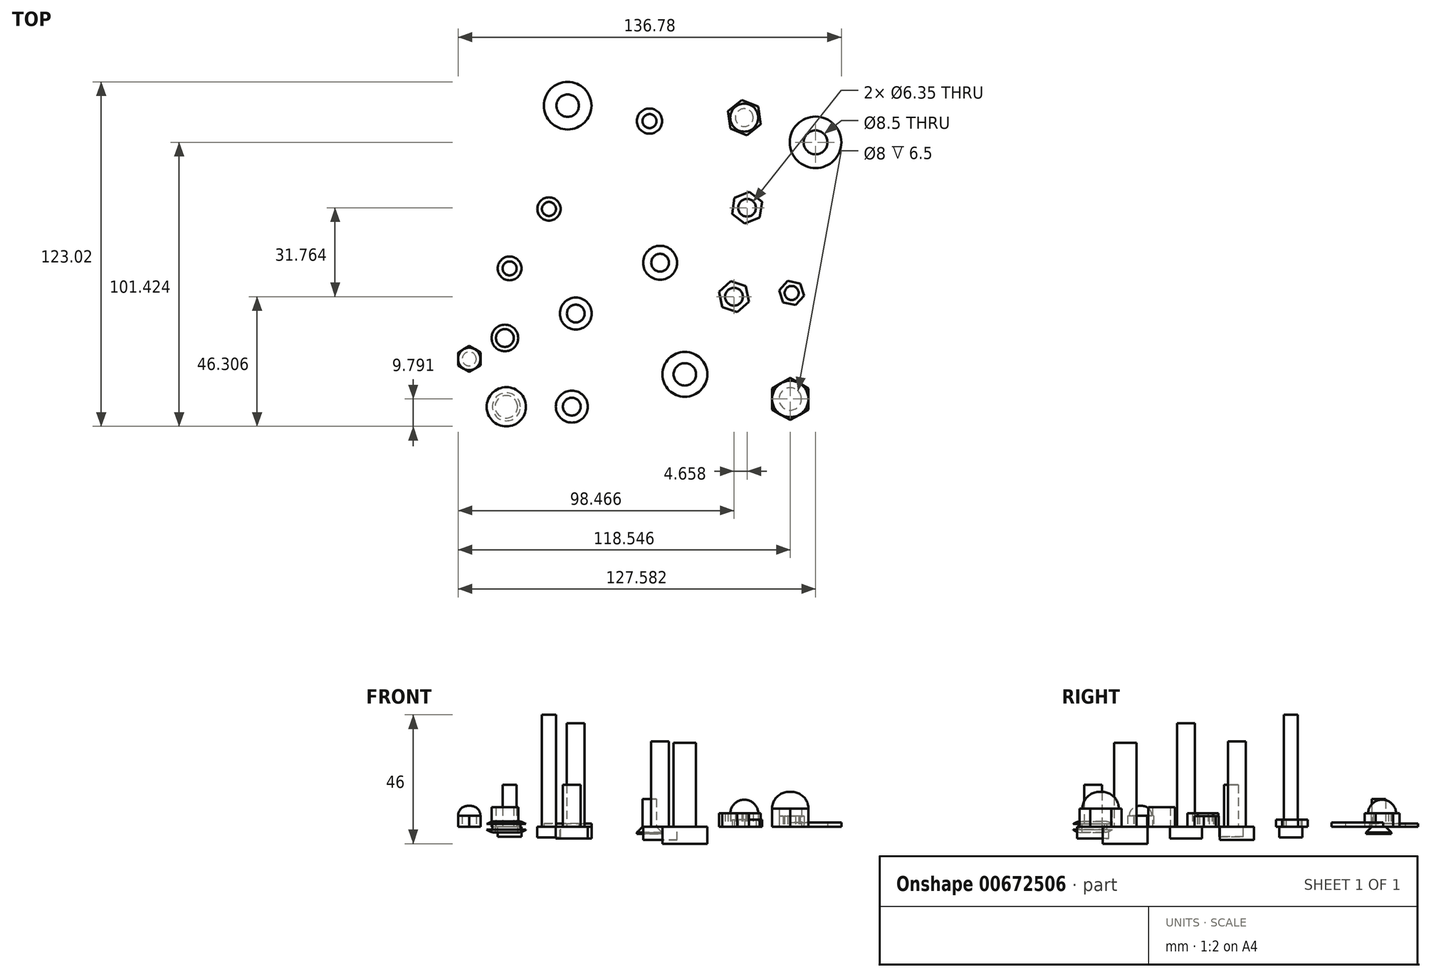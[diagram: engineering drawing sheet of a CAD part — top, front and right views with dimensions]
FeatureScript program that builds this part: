
annotation { "Feature Type Name" : "Feature", "Feature Type Description" : "" }
export const myFeature = defineFeature(function(context is Context, id is Id, definition is map)
    precondition{}
    {
        {
            var Q0;
            Q0=qCreatedBy(makeId("Top.planeOp"),FACE);
            var sketch = newSketch(context, id + "F0", { "sketchPlane" : qUnion([Q0])});
            skCircle(sketch, "E0", {"center": v(0, 0) * mm, "radius": 3.18 * mm});
            skSolve(sketch);
        }
        {
            var Q0;
            Q0 = qSketchRegion(id + "F0", true);
            extrude(context, id + "F1", {"entities" : qUnion([Q0]), "depth" : 30.5 * mm, "offsetDistance" : 25 * mm});
        }
        {
            var Q0;
            Q0=makeQuery(id+"F1.opExtrude","CAP_FACE",FACE,{"disambiguationData":[OSD([sQuery(id+"F0.wireOp",EDGE,"E0")])],"isStart":true});
            var sketch = newSketch(context, id + "F2", { "sketchPlane" : qUnion([Q0])});
            skCircle(sketch, "E1", {"center": v(0, 0) * mm, "radius": 6.07 * mm});
            skSolve(sketch);
        }
        {
            var Q0;
            Q0 = qSketchRegion(id + "F2", true);
            extrude(context, id + "F3", {"entities" : qUnion([Q0]), "operationType" : NewBodyOperationType.ADD, "depth" : 4.7 * mm, "offsetDistance" : 25 * mm});
        }
        {
            var Q0;
            Q0=qCreatedBy(makeId("Top.planeOp"),FACE);
            var sketch = newSketch(context, id + "F4", { "sketchPlane" : qUnion([Q0])});
            skCircle(sketch, "E2.cCircle", {"center": v(26.36, -12.11) * mm, "radius": 4.9 * mm, "construction": true});
            skLineSegment(sketch, "E2.0", {"start": v(21, -10.32) * mm, "end": v(25.23, -6.57) * mm});
            skLineSegment(sketch, "E2.1", {"start": v(25.23, -6.57) * mm, "end": v(30.6, -8.37) * mm});
            skLineSegment(sketch, "E2.2", {"start": v(30.6, -8.37) * mm, "end": v(31.72, -13.91) * mm});
            skLineSegment(sketch, "E2.3", {"start": v(31.72, -13.91) * mm, "end": v(27.48, -17.66) * mm});
            skLineSegment(sketch, "E2.4", {"start": v(27.48, -17.66) * mm, "end": v(22.12, -15.86) * mm});
            skLineSegment(sketch, "E2.5", {"start": v(22.12, -15.86) * mm, "end": v(21, -10.32) * mm});
            skPoint(sketch, "E2.0.midPoint", {"position": v(23.11, -8.44) * mm});
            skCircle(sketch, "E3", {"center": v(26.36, -12.11) * mm, "radius": 3.17 * mm});
            skSolve(sketch);
        }
        {
            var Q0;
            Q0 = qSketchRegion(id + "F4", true);
            extrude(context, id + "F5", {"entities" : qUnion([Q0]), "depth" : 4.9 * mm, "offsetDistance" : 25 * mm});
        }
        {
            var Q0;
            Q0=qCreatedBy(makeId("Top.planeOp"),FACE);
            var sketch = newSketch(context, id + "F6", { "sketchPlane" : qUnion([Q0])});
            skCircle(sketch, "E4", {"center": v(-30.1, -18.13) * mm, "radius": 3.17 * mm});
            skSolve(sketch);
        }
        {
            var Q0;
            Q0 = qSketchRegion(id + "F6", true);
            extrude(context, id + "F7", {"entities" : qUnion([Q0]), "depth" : 37 * mm, "offsetDistance" : 25 * mm});
        }
        {
            var Q0;
            Q0=makeQuery(id+"F7.opExtrude","CAP_FACE",FACE,{"disambiguationData":[OSD([sQuery(id+"F6.wireOp",EDGE,"E4")])],"isStart":true});
            var sketch = newSketch(context, id + "F8", { "sketchPlane" : qUnion([Q0])});
            skCircle(sketch, "E5", {"center": v(-30.1, 18.13) * mm, "radius": 5.7 * mm});
            skSolve(sketch);
        }
        {
            var Q0;
            Q0 = qSketchRegion(id + "F8", true);
            extrude(context, id + "F9", {"entities" : qUnion([Q0]), "operationType" : NewBodyOperationType.ADD, "depth" : 4.1 * mm, "offsetDistance" : 25 * mm});
        }
        {
            var Q0;
            Q0=qCreatedBy(makeId("Top.planeOp"),FACE);
            var sketch = newSketch(context, id + "F10", { "sketchPlane" : qUnion([Q0])});
            skCircle(sketch, "E6.cCircle", {"center": v(31.01, 19.65) * mm, "radius": 4.97 * mm, "construction": true});
            skLineSegment(sketch, "E6.0", {"start": v(31.81, 25.34) * mm, "end": v(36.34, 21.8) * mm});
            skLineSegment(sketch, "E6.1", {"start": v(36.34, 21.8) * mm, "end": v(35.54, 16.12) * mm});
            skLineSegment(sketch, "E6.2", {"start": v(35.54, 16.12) * mm, "end": v(30.22, 13.96) * mm});
            skLineSegment(sketch, "E6.3", {"start": v(30.22, 13.96) * mm, "end": v(25.69, 17.5) * mm});
            skLineSegment(sketch, "E6.4", {"start": v(25.69, 17.5) * mm, "end": v(26.49, 23.18) * mm});
            skLineSegment(sketch, "E6.5", {"start": v(26.49, 23.18) * mm, "end": v(31.81, 25.34) * mm});
            skPoint(sketch, "E6.0.midPoint", {"position": v(34.07, 23.57) * mm});
            skCircle(sketch, "E7", {"center": v(31.01, 19.65) * mm, "radius": 3.17 * mm});
            skSolve(sketch);
        }
        {
            var Q0;
            Q0 = qSketchRegion(id + "F10", true);
            extrude(context, id + "F11", {"entities" : qUnion([Q0]), "depth" : 2.6 * mm, "offsetDistance" : 25 * mm});
        }
        {
            var Q0;
            Q0=qCreatedBy(makeId("Top.planeOp"),FACE);
            var sketch = newSketch(context, id + "F12", { "sketchPlane" : qUnion([Q0])});
            skCircle(sketch, "E8.cCircle", {"center": v(46.94, -10.79) * mm, "radius": 3.92 * mm, "construction": true});
            skLineSegment(sketch, "E8.0", {"start": v(45.55, -6.47) * mm, "end": v(49.98, -7.43) * mm});
            skLineSegment(sketch, "E8.1", {"start": v(49.98, -7.43) * mm, "end": v(51.37, -11.74) * mm});
            skLineSegment(sketch, "E8.2", {"start": v(51.37, -11.74) * mm, "end": v(48.32, -15.1) * mm});
            skLineSegment(sketch, "E8.3", {"start": v(48.32, -15.1) * mm, "end": v(43.9, -14.15) * mm});
            skLineSegment(sketch, "E8.4", {"start": v(43.9, -14.15) * mm, "end": v(42.5, -9.83) * mm});
            skLineSegment(sketch, "E8.5", {"start": v(42.5, -9.83) * mm, "end": v(45.55, -6.47) * mm});
            skPoint(sketch, "E8.0.midPoint", {"position": v(47.77, -6.95) * mm});
            skCircle(sketch, "E9", {"center": v(46.94, -10.79) * mm, "radius": 2.5 * mm});
            skSolve(sketch);
        }
        {
            var Q0;
            Q0 = qSketchRegion(id + "F12", true);
            extrude(context, id + "F13", {"entities" : qUnion([Q0]), "depth" : 3.9 * mm, "offsetDistance" : 25 * mm});
        }
        {
            var Q0;
            Q0=qCreatedBy(makeId("Top.planeOp"),FACE);
            var sketch = newSketch(context, id + "F14", { "sketchPlane" : qUnion([Q0])});
            skCircle(sketch, "E10", {"center": v(-39.67, 19.21) * mm, "radius": 2.5 * mm});
            skSolve(sketch);
        }
        {
            var Q0;
            Q0 = qSketchRegion(id + "F14", true);
            extrude(context, id + "F15", {"entities" : qUnion([Q0]), "depth" : 40 * mm, "offsetDistance" : 25 * mm});
        }
        {
            var Q0;
            Q0=makeQuery(id+"F15.opExtrude","CAP_FACE",FACE,{"disambiguationData":[OSD([sQuery(id+"F14.wireOp",EDGE,"E10")])],"isStart":true});
            var sketch = newSketch(context, id + "F16", { "sketchPlane" : qUnion([Q0])});
            skCircle(sketch, "E11", {"center": v(-39.67, -19.21) * mm, "radius": 4.15 * mm});
            skSolve(sketch);
        }
        {
            var Q0;
            Q0 = qSketchRegion(id + "F16", true);
            extrude(context, id + "F17", {"entities" : qUnion([Q0]), "operationType" : NewBodyOperationType.ADD, "depth" : 3.7 * mm, "offsetDistance" : 25 * mm});
        }
        {
            var Q0;
            Q0=qCreatedBy(makeId("Top.planeOp"),FACE);
            var sketch = newSketch(context, id + "F18", { "sketchPlane" : qUnion([Q0])});
            skCircle(sketch, "E12", {"center": v(-53.72, -2.01) * mm, "radius": 2.5 * mm});
            skSolve(sketch);
        }
        {
            var Q0;
            Q0 = qSketchRegion(id + "F18", true);
            extrude(context, id + "F19", {"entities" : qUnion([Q0]), "depth" : 15 * mm, "offsetDistance" : 25 * mm});
        }
        {
            var Q0;
            Q0=makeQuery(id+"F19.opExtrude","CAP_FACE",FACE,{"disambiguationData":[OSD([sQuery(id+"F18.wireOp",EDGE,"E12")])],"isStart":true});
            var sketch = newSketch(context, id + "F20", { "sketchPlane" : qUnion([Q0])});
            skCircle(sketch, "E13", {"center": v(-53.72, 2.01) * mm, "radius": 4.25 * mm});
            skSolve(sketch);
        }
        {
            var Q0;
            Q0 = qSketchRegion(id + "F20", true);
            extrude(context, id + "F21", {"entities" : qUnion([Q0]), "operationType" : NewBodyOperationType.ADD, "depth" : 3.5 * mm, "offsetDistance" : 25 * mm});
        }
        {
            var Q0;
            Q0=qCreatedBy(makeId("Top.planeOp"),FACE);
            var sketch = newSketch(context, id + "F22", { "sketchPlane" : qUnion([Q0])});
            skCircle(sketch, "E14.cCircle", {"center": v(30.03, 51.82) * mm, "radius": 5.47 * mm, "construction": true});
            skLineSegment(sketch, "E14.0", {"start": v(24.15, 54.16) * mm, "end": v(29.11, 58.08) * mm});
            skLineSegment(sketch, "E14.1", {"start": v(29.11, 58.08) * mm, "end": v(34.99, 55.74) * mm});
            skLineSegment(sketch, "E14.2", {"start": v(34.99, 55.74) * mm, "end": v(35.9, 49.48) * mm});
            skLineSegment(sketch, "E14.3", {"start": v(35.9, 49.48) * mm, "end": v(30.94, 45.57) * mm});
            skLineSegment(sketch, "E14.4", {"start": v(30.94, 45.57) * mm, "end": v(25.06, 47.9) * mm});
            skLineSegment(sketch, "E14.5", {"start": v(25.06, 47.9) * mm, "end": v(24.15, 54.16) * mm});
            skPoint(sketch, "E14.0.midPoint", {"position": v(26.63, 56.12) * mm});
            skCircle(sketch, "E15", {"center": v(30.03, 51.82) * mm, "radius": 3.17 * mm});
            skSolve(sketch);
        }
        {
            var Q0;
            Q0 = qSketchRegion(id + "F22", true);
            extrude(context, id + "F23", {"entities" : qUnion([Q0]), "depth" : 4.9 * mm, "offsetDistance" : 25 * mm});
        }
        {
            var Q0;
            Q0=makeQuery(id+"F23.opExtrude","CAP_FACE",FACE,{"disambiguationData":[OSD([sQuery(id+"F22.wireOp",EDGE,"E14.0"),sQuery(id+"F22.wireOp",EDGE,"E14.1"),sQuery(id+"F22.wireOp",EDGE,"E14.2"),sQuery(id+"F22.wireOp",EDGE,"E14.3"),sQuery(id+"F22.wireOp",EDGE,"E14.4"),sQuery(id+"F22.wireOp",EDGE,"E14.5"),sQuery(id+"F22.wireOp",EDGE,"E15")])],"isStart":false});
            var sketch = newSketch(context, id + "F24", { "sketchPlane" : qUnion([Q0])});
            skCircle(sketch, "E16", {"center": v(30.03, 51.82) * mm, "radius": 5 * mm});
            skSolve(sketch);
        }
        {
            var Q0;
            Q0 = qSketchRegion(id + "F24", true);
            extrude(context, id + "F25", {"entities" : qUnion([Q0]), "operationType" : NewBodyOperationType.ADD, "depth" : 4.8 * mm, "offsetDistance" : 25 * mm});
        }
        {
            var Q0;
            Q0=makeQuery(id+"F25.opExtrude","CAP_EDGE",EDGE,{"disambiguationData":[OSD([sQuery(id+"F24.wireOp",EDGE,"E16")])],"isStart":false});
            fillet(context, id + "F26", {"entities" : qUnion([Q0]), "radius" : 5 * mm, "tangentPropagation" : true, "allowEdgeOverflow" : false});
        }
        {
            var Q0;
            Q0=qCreatedBy(makeId("Top.planeOp"),FACE);
            var sketch = newSketch(context, id + "F27", { "sketchPlane" : qUnion([Q0])});
            skCircle(sketch, "E17", {"center": v(-54.88, -51.42) * mm, "radius": 4 * mm});
            skCircle(sketch, "E18", {"center": v(-54.88, -51.42) * mm, "radius": 5 * mm});
            skSolve(sketch);
        }
        {
            var Q0;
            Q0 = qSketchRegion(id + "F27", true);
            extrude(context, id + "F28", {"entities" : qUnion([Q0]), "endBound" : BoundingType.SYMMETRIC, "depth" : 2 * mm, "offsetDistance" : 25 * mm});
        }
        {
            var Q0;
            Q0=makeQuery(id+"F28.opExtrude","CAP_FACE",FACE,{"disambiguationData":[OSD([sQuery(id+"F27.wireOp",EDGE,"E17"),sQuery(id+"F27.wireOp",EDGE,"E18")])],"isStart":false});
            var sketch = newSketch(context, id + "F29", { "sketchPlane" : qUnion([Q0])});
            skCircle(sketch, "E19", {"center": v(-54.88, -51.42) * mm, "radius": 7 * mm});
            skSolve(sketch);
        }
        {
            var Q0;
            Q0 = qSketchRegion(id + "F29", true);
            extrude(context, id + "F30", {"entities" : qUnion([Q0]), "operationType" : NewBodyOperationType.ADD, "depth" : 1 * mm, "offsetDistance" : 25 * mm});
        }
        {
            var Q0;
            Q0=makeQuery(id+"F30.opExtrude","CAP_EDGE",EDGE,{"disambiguationData":[OSD([sQuery(id+"F29.wireOp",EDGE,"E19")])],"isStart":false});
            fillet(context, id + "F31", {"entities" : qUnion([Q0]), "radius" : 5 * mm, "tangentPropagation" : true, "allowEdgeOverflow" : false});
        }
        {
            var Q0;
            Q0=makeQuery(id+"F28.opExtrude","CAP_FACE",FACE,{"disambiguationData":[OSD([sQuery(id+"F27.wireOp",EDGE,"E17"),sQuery(id+"F27.wireOp",EDGE,"E18")])],"isStart":true});
            var sketch = newSketch(context, id + "F32", { "sketchPlane" : qUnion([Q0])});
            skCircle(sketch, "E20", {"center": v(-54.88, 51.42) * mm, "radius": 7 * mm});
            skCircle(sketch, "E21", {"center": v(-54.88, 51.42) * mm, "radius": 4 * mm});
            skSolve(sketch);
        }
        {
            var Q0;
            Q0 = qSketchRegion(id + "F32", true);
            extrude(context, id + "F33", {"entities" : qUnion([Q0]), "operationType" : NewBodyOperationType.ADD, "depth" : 1 * mm, "offsetDistance" : 25 * mm});
        }
        {
            var Q0;
            Q0=makeQuery(id+"F33.opExtrude","CAP_EDGE",EDGE,{"disambiguationData":[OSD([sQuery(id+"F32.wireOp",EDGE,"E20")])],"isStart":false});
            fillet(context, id + "F34", {"entities" : qUnion([Q0]), "radius" : 5 * mm, "tangentPropagation" : true, "allowEdgeOverflow" : false});
        }
        {
            var Q0;
            Q0=qCreatedBy(makeId("Top.planeOp"),FACE);
            var sketch = newSketch(context, id + "F35", { "sketchPlane" : qUnion([Q0])});
            skCircle(sketch, "E22", {"center": v(8.82, -39.83) * mm, "radius": 4 * mm});
            skSolve(sketch);
        }
        {
            var Q0;
            Q0 = qSketchRegion(id + "F35", true);
            extrude(context, id + "F36", {"entities" : qUnion([Q0]), "depth" : 30 * mm, "offsetDistance" : 25 * mm});
        }
        {
            var Q0;
            Q0=makeQuery(id+"F36.opExtrude","CAP_FACE",FACE,{"disambiguationData":[OSD([sQuery(id+"F35.wireOp",EDGE,"E22")])],"isStart":true});
            var sketch = newSketch(context, id + "F37", { "sketchPlane" : qUnion([Q0])});
            skCircle(sketch, "E23", {"center": v(8.82, 39.83) * mm, "radius": 8 * mm});
            skSolve(sketch);
        }
        {
            var Q0;
            Q0 = qSketchRegion(id + "F37", true);
            extrude(context, id + "F38", {"entities" : qUnion([Q0]), "operationType" : NewBodyOperationType.ADD, "depth" : 6 * mm, "offsetDistance" : 25 * mm});
        }
        {
            var Q0;
            Q0=qCreatedBy(makeId("Top.planeOp"),FACE);
            var sketch = newSketch(context, id + "F39", { "sketchPlane" : qUnion([Q0])});
            skCircle(sketch, "E24.cCircle", {"center": v(46.44, -48.63) * mm, "radius": 6.5 * mm, "construction": true});
            skLineSegment(sketch, "E24.0", {"start": v(39.94, -52.38) * mm, "end": v(39.94, -44.88) * mm});
            skLineSegment(sketch, "E24.1", {"start": v(39.94, -44.88) * mm, "end": v(46.44, -41.12) * mm});
            skLineSegment(sketch, "E24.2", {"start": v(46.44, -41.12) * mm, "end": v(52.94, -44.88) * mm});
            skLineSegment(sketch, "E24.3", {"start": v(52.94, -44.88) * mm, "end": v(52.94, -52.38) * mm});
            skLineSegment(sketch, "E24.4", {"start": v(52.94, -52.38) * mm, "end": v(46.44, -56.13) * mm});
            skLineSegment(sketch, "E24.5", {"start": v(46.44, -56.13) * mm, "end": v(39.94, -52.38) * mm});
            skPoint(sketch, "E24.0.midPoint", {"position": v(39.94, -48.63) * mm});
            skCircle(sketch, "E25", {"center": v(46.44, -48.63) * mm, "radius": 4 * mm});
            skSolve(sketch);
        }
        {
            var Q0;
            Q0 = qSketchRegion(id + "F39", true);
            extrude(context, id + "F40", {"entities" : qUnion([Q0]), "depth" : 6.5 * mm, "offsetDistance" : 25 * mm});
        }
        {
            var Q0;
            Q0=makeQuery(id+"F40.opExtrude","CAP_FACE",FACE,{"disambiguationData":[OSD([sQuery(id+"F39.wireOp",EDGE,"E24.0"),sQuery(id+"F39.wireOp",EDGE,"E24.1"),sQuery(id+"F39.wireOp",EDGE,"E24.2"),sQuery(id+"F39.wireOp",EDGE,"E24.3"),sQuery(id+"F39.wireOp",EDGE,"E24.4"),sQuery(id+"F39.wireOp",EDGE,"E24.5"),sQuery(id+"F39.wireOp",EDGE,"E25")])],"isStart":false});
            var sketch = newSketch(context, id + "F41", { "sketchPlane" : qUnion([Q0])});
            skCircle(sketch, "E26", {"center": v(46.44, -48.63) * mm, "radius": 6.5 * mm});
            skSolve(sketch);
        }
        {
            var Q0;
            Q0 = qSketchRegion(id + "F41", true);
            extrude(context, id + "F42", {"entities" : qUnion([Q0]), "operationType" : NewBodyOperationType.ADD, "depth" : 6 * mm, "offsetDistance" : 25 * mm});
        }
        {
            var Q0;
            Q0=makeQuery(id+"F42.opExtrude","CAP_EDGE",EDGE,{"disambiguationData":[OSD([sQuery(id+"F41.wireOp",EDGE,"E26")])],"isStart":false});
            fillet(context, id + "F43", {"entities" : qUnion([Q0]), "radius" : 6 * mm, "tangentPropagation" : true, "allowEdgeOverflow" : false});
        }
        {
            var Q0;
            Q0=qCreatedBy(makeId("Top.planeOp"),FACE);
            var sketch = newSketch(context, id + "F44", { "sketchPlane" : qUnion([Q0])});
            skCircle(sketch, "E27", {"center": v(-33, 56.1) * mm, "radius": 4 * mm});
            skCircle(sketch, "E28", {"center": v(-33, 56.1) * mm, "radius": 8.5 * mm});
            skSolve(sketch);
        }
        {
            var Q0;
            Q0 = qSketchRegion(id + "F44", true);
            extrude(context, id + "F45", {"entities" : qUnion([Q0]), "depth" : 1.2 * mm, "offsetDistance" : 25 * mm});
        }
        {
            var Q0;
            Q0=qCreatedBy(makeId("Top.planeOp"),FACE);
            var sketch = newSketch(context, id + "F46", { "sketchPlane" : qUnion([Q0])});
            skCircle(sketch, "E29", {"center": v(-55.4, -26.86) * mm, "radius": 4.75 * mm});
            skCircle(sketch, "E30", {"center": v(-55.4, -26.86) * mm, "radius": 3.17 * mm});
            skSolve(sketch);
        }
        {
            var Q0;
            Q0 = qSketchRegion(id + "F46", true);
            extrude(context, id + "F47", {"entities" : qUnion([Q0]), "depth" : 7 * mm, "offsetDistance" : 25 * mm});
        }
        {
            var Q0;
            Q0=qCreatedBy(makeId("Top.planeOp"),FACE);
            var sketch = newSketch(context, id + "F48", { "sketchPlane" : qUnion([Q0])});
            skCircle(sketch, "E31", {"center": v(-31.51, -51.36) * mm, "radius": 3.17 * mm});
            skSolve(sketch);
        }
        {
            var Q0;
            Q0 = qSketchRegion(id + "F48", true);
            extrude(context, id + "F49", {"entities" : qUnion([Q0]), "depth" : 15 * mm, "offsetDistance" : 25 * mm});
        }
        {
            var Q0;
            Q0=makeQuery(id+"F49.opExtrude","CAP_FACE",FACE,{"disambiguationData":[OSD([sQuery(id+"F48.wireOp",EDGE,"E31")])],"isStart":true});
            var sketch = newSketch(context, id + "F50", { "sketchPlane" : qUnion([Q0])});
            skCircle(sketch, "E32", {"center": v(-31.51, 51.36) * mm, "radius": 5.7 * mm});
            skSolve(sketch);
        }
        {
            var Q0;
            Q0 = qSketchRegion(id + "F50", true);
            extrude(context, id + "F51", {"entities" : qUnion([Q0]), "operationType" : NewBodyOperationType.ADD, "depth" : 4.1 * mm, "offsetDistance" : 25 * mm});
        }
        {
            var Q0;
            Q0=qCreatedBy(makeId("Top.planeOp"),FACE);
            var sketch = newSketch(context, id + "F52", { "sketchPlane" : qUnion([Q0])});
            skCircle(sketch, "E33", {"center": v(55.47, 43) * mm, "radius": 9.2 * mm});
            skCircle(sketch, "E34", {"center": v(55.47, 43) * mm, "radius": 4.25 * mm});
            skSolve(sketch);
        }
        {
            var Q0;
            Q0 = qSketchRegion(id + "F52", true);
            extrude(context, id + "F53", {"entities" : qUnion([Q0]), "depth" : 1.6 * mm, "offsetDistance" : 25 * mm});
        }
        {
            var Q0;
            Q0=qCreatedBy(makeId("Top.planeOp"),FACE);
            var sketch = newSketch(context, id + "F54", { "sketchPlane" : qUnion([Q0])});
            skCircle(sketch, "E35.cCircle", {"center": v(-68.11, -34.33) * mm, "radius": 4 * mm, "construction": true});
            skLineSegment(sketch, "E35.0", {"start": v(-72.11, -36.64) * mm, "end": v(-72.11, -32.02) * mm});
            skLineSegment(sketch, "E35.1", {"start": v(-72.11, -32.02) * mm, "end": v(-68.11, -29.7) * mm});
            skLineSegment(sketch, "E35.2", {"start": v(-68.11, -29.7) * mm, "end": v(-64.11, -32.02) * mm});
            skLineSegment(sketch, "E35.3", {"start": v(-64.11, -32.02) * mm, "end": v(-64.11, -36.64) * mm});
            skLineSegment(sketch, "E35.4", {"start": v(-64.11, -36.64) * mm, "end": v(-68.11, -38.95) * mm});
            skLineSegment(sketch, "E35.5", {"start": v(-68.11, -38.95) * mm, "end": v(-72.11, -36.64) * mm});
            skPoint(sketch, "E35.0.midPoint", {"position": v(-72.11, -34.33) * mm});
            skCircle(sketch, "E36", {"center": v(-68.11, -34.33) * mm, "radius": 2.5 * mm});
            skSolve(sketch);
        }
        {
            var Q0;
            Q0 = qSketchRegion(id + "F54", true);
            extrude(context, id + "F55", {"entities" : qUnion([Q0]), "depth" : 4 * mm, "offsetDistance" : 25 * mm});
        }
        {
            var Q0;
            Q0=makeQuery(id+"F55.opExtrude","CAP_FACE",FACE,{"disambiguationData":[OSD([sQuery(id+"F54.wireOp",EDGE,"E35.0"),sQuery(id+"F54.wireOp",EDGE,"E35.1"),sQuery(id+"F54.wireOp",EDGE,"E35.2"),sQuery(id+"F54.wireOp",EDGE,"E35.3"),sQuery(id+"F54.wireOp",EDGE,"E35.4"),sQuery(id+"F54.wireOp",EDGE,"E35.5"),sQuery(id+"F54.wireOp",EDGE,"E36")])],"isStart":false});
            var sketch = newSketch(context, id + "F56", { "sketchPlane" : qUnion([Q0])});
            skCircle(sketch, "E37", {"center": v(-68.11, -34.33) * mm, "radius": 4 * mm});
            skSolve(sketch);
        }
        {
            var Q0;
            Q0 = qSketchRegion(id + "F56", true);
            extrude(context, id + "F57", {"entities" : qUnion([Q0]), "operationType" : NewBodyOperationType.ADD, "depth" : 3.5 * mm, "offsetDistance" : 25 * mm});
        }
        {
            var Q0;
            Q0=makeQuery(id+"F57.opExtrude","CAP_EDGE",EDGE,{"disambiguationData":[OSD([sQuery(id+"F56.wireOp",EDGE,"E37")])],"isStart":false});
            fillet(context, id + "F58", {"entities" : qUnion([Q0]), "radius" : 3.5 * mm, "tangentPropagation" : true, "allowEdgeOverflow" : false});
        }
        {
            var Q0;
            Q0=qCreatedBy(makeId("Top.planeOp"),FACE);
            var sketch = newSketch(context, id + "F59", { "sketchPlane" : qUnion([Q0])});
            skCircle(sketch, "E38", {"center": v(-3.79, 50.59) * mm, "radius": 2.5 * mm});
            skSolve(sketch);
        }
        {
            var Q0;
            Q0 = qSketchRegion(id + "F59", true);
            extrude(context, id + "F60", {"entities" : qUnion([Q0]), "depth" : 10 * mm, "offsetDistance" : 25 * mm});
        }
        {
            var Q0;
            Q0=makeQuery(id+"F60.opExtrude","CAP_FACE",FACE,{"disambiguationData":[OSD([sQuery(id+"F59.wireOp",EDGE,"E38")])],"isStart":true});
            var sketch = newSketch(context, id + "F61", { "sketchPlane" : qUnion([Q0])});
            skCircle(sketch, "E39", {"center": v(-3.79, -50.59) * mm, "radius": 4.5 * mm});
            skSolve(sketch);
        }
        {
            var Q0;
            Q0 = qSketchRegion(id + "F61", true);
            extrude(context, id + "F62", {"entities" : qUnion([Q0]), "operationType" : NewBodyOperationType.ADD, "depth" : 2.5 * mm, "offsetDistance" : 25 * mm});
        }
        {
            var Q0;
            Q0=makeQuery(id+"F62.opExtrude","CAP_EDGE",EDGE,{"disambiguationData":[OSD([sQuery(id+"F61.wireOp",EDGE,"E39")])],"isStart":true});
            chamfer(context, id + "F63", {"entities" : qUnion([Q0]), "width" : 2 * mm, "tangentPropagation" : true});
        }
    });
